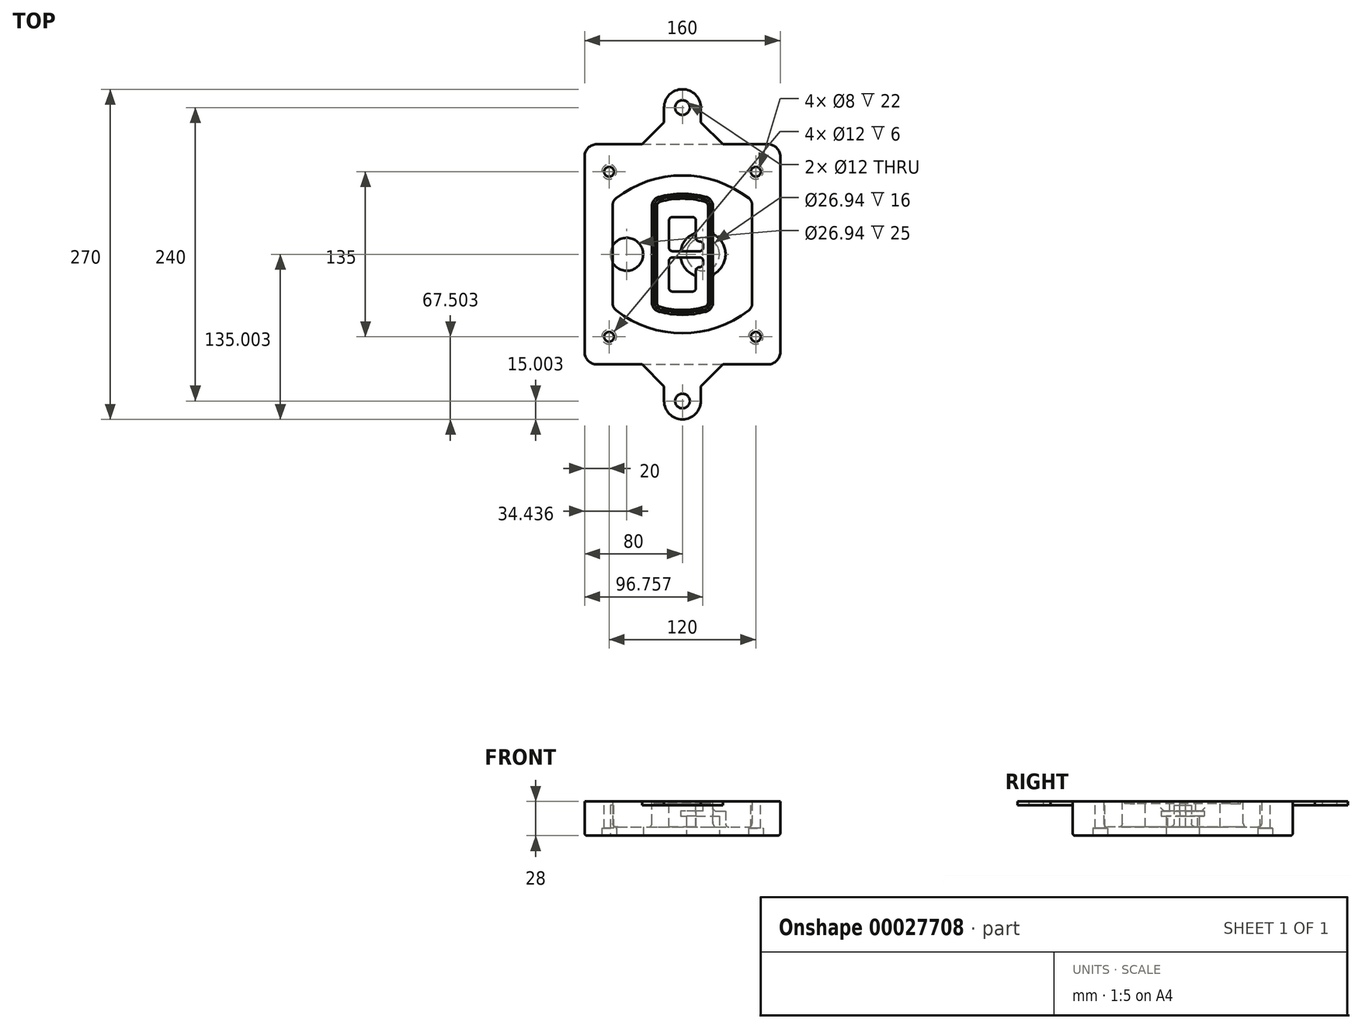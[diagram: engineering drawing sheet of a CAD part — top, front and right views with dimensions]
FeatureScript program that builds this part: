
annotation { "Feature Type Name" : "Feature", "Feature Type Description" : "" }
export const myFeature = defineFeature(function(context is Context, id is Id, definition is map)
    precondition{}
    {
        {
            var Q0;
            Q0=qCreatedBy(makeId("Top.planeOp"),FACE);
            var sketch = newSketch(context, id + "F0", { "sketchPlane" : qUnion([Q0])});
            skPoint(sketch, "E0.rect.middle", {"position": v(0, 0) * mm});
            skLineSegment(sketch, "E1.bottom", {"start": v(24.05, 28.38) * mm, "end": v(164.05, 28.38) * mm});
            skLineSegment(sketch, "E1.top", {"start": v(24.05, 208.38) * mm, "end": v(164.05, 208.38) * mm});
            skLineSegment(sketch, "E1.left", {"start": v(14.05, 38.38) * mm, "end": v(14.05, 198.38) * mm});
            skLineSegment(sketch, "E1.right", {"start": v(174.05, 38.38) * mm, "end": v(174.05, 198.38) * mm});
            skLineSegment(sketch, "E2", {"start": v(14.05, 208.38) * mm, "end": v(174.05, 28.38) * mm, "construction": true});
            skLineSegment(sketch, "E3", {"start": v(174.05, 208.38) * mm, "end": v(14.05, 28.38) * mm, "construction": true});
            skCircle(sketch, "E4", {"center": v(34.05, 185.88) * mm, "radius": 4 * mm});
            skCircle(sketch, "E5", {"center": v(154.05, 185.88) * mm, "radius": 4 * mm});
            skCircle(sketch, "E6", {"center": v(154.05, 50.88) * mm, "radius": 4 * mm});
            skCircle(sketch, "E7", {"center": v(34.05, 50.88) * mm, "radius": 4 * mm});
            skLineSegment(sketch, "E8", {"start": v(34.05, 185.88) * mm, "end": v(154.05, 185.88) * mm, "construction": true});
            skLineSegment(sketch, "E9", {"start": v(154.05, 185.88) * mm, "end": v(154.05, 50.88) * mm, "construction": true});
            skLineSegment(sketch, "E10", {"start": v(154.05, 50.88) * mm, "end": v(34.05, 50.88) * mm, "construction": true});
            skLineSegment(sketch, "E11", {"start": v(34.05, 50.88) * mm, "end": v(34.05, 185.88) * mm, "construction": true});
            skLineSegment(sketch, "E12", {"start": v(34.05, 158.68) * mm, "end": v(34.05, 78.09) * mm});
            skLineSegment(sketch, "E13", {"start": v(154.05, 158.68) * mm, "end": v(154.05, 78.09) * mm});
            skArc(sketch, "E14", {"start": v(150.2, 166.56) * mm, "mid": v(94.05, 185.88) * mm, "end": v(37.9, 166.56) * mm});
            skArc(sketch, "E15", {"start": v(37.9, 70.2) * mm, "mid": v(94.05, 50.88) * mm, "end": v(150.2, 70.2) * mm});
            skLineSegment(sketch, "E16", {"start": v(34.05, 118.38) * mm, "end": v(154.05, 118.38) * mm, "construction": true});
            skPoint(sketch, "E17.visualSharp", {"position": v(34.05, 73.38) * mm});
            skArc(sketch, "E17.filletArc", {"start": v(34.05, 78.09) * mm, "mid": v(35.06, 73.7) * mm, "end": v(37.9, 70.2) * mm});
            skPoint(sketch, "E18.visualSharp", {"position": v(34.05, 163.38) * mm});
            skArc(sketch, "E18.filletArc", {"start": v(37.9, 166.56) * mm, "mid": v(35.06, 163.06) * mm, "end": v(34.05, 158.68) * mm});
            skPoint(sketch, "E19.visualSharp", {"position": v(154.05, 163.38) * mm});
            skArc(sketch, "E19.filletArc", {"start": v(154.05, 158.68) * mm, "mid": v(153.04, 163.06) * mm, "end": v(150.2, 166.56) * mm});
            skPoint(sketch, "E20.visualSharp", {"position": v(154.05, 73.38) * mm});
            skArc(sketch, "E20.filletArc", {"start": v(150.2, 70.2) * mm, "mid": v(153.04, 73.7) * mm, "end": v(154.05, 78.09) * mm});
            skPoint(sketch, "E21.visualSharp", {"position": v(14.05, 208.38) * mm});
            skArc(sketch, "E21.filletArc", {"start": v(24.05, 208.38) * mm, "mid": v(16.98, 205.45) * mm, "end": v(14.05, 198.38) * mm});
            skPoint(sketch, "E22.visualSharp", {"position": v(174.05, 208.38) * mm});
            skArc(sketch, "E22.filletArc", {"start": v(174.05, 198.38) * mm, "mid": v(171.12, 205.45) * mm, "end": v(164.05, 208.38) * mm});
            skPoint(sketch, "E23.visualSharp", {"position": v(174.05, 28.38) * mm});
            skArc(sketch, "E23.filletArc", {"start": v(164.05, 28.38) * mm, "mid": v(171.12, 31.31) * mm, "end": v(174.05, 38.38) * mm});
            skPoint(sketch, "E24.visualSharp", {"position": v(14.05, 28.38) * mm});
            skArc(sketch, "E24.filletArc", {"start": v(14.05, 38.38) * mm, "mid": v(16.98, 31.31) * mm, "end": v(24.05, 28.38) * mm});
            skArc(sketch, "E25.0", {"start": v(151.05, 158.68) * mm, "mid": v(150.34, 161.75) * mm, "end": v(148.36, 164.2) * mm});
            skLineSegment(sketch, "E25.1", {"start": v(151.05, 158.68) * mm, "end": v(151.05, 78.09) * mm});
            skArc(sketch, "E25.2", {"start": v(148.36, 72.57) * mm, "mid": v(150.34, 75.02) * mm, "end": v(151.05, 78.09) * mm});
            skArc(sketch, "E25.3", {"start": v(39.74, 72.57) * mm, "mid": v(94.05, 53.88) * mm, "end": v(148.36, 72.57) * mm});
            skArc(sketch, "E25.4", {"start": v(37.05, 78.09) * mm, "mid": v(37.76, 75.02) * mm, "end": v(39.74, 72.57) * mm});
            skArc(sketch, "E25.5", {"start": v(148.36, 164.2) * mm, "mid": v(94.05, 182.88) * mm, "end": v(39.74, 164.2) * mm});
            skLineSegment(sketch, "E25.6", {"start": v(37.05, 158.68) * mm, "end": v(37.05, 78.09) * mm});
            skArc(sketch, "E25.7", {"start": v(39.74, 164.2) * mm, "mid": v(37.76, 161.75) * mm, "end": v(37.05, 158.68) * mm});
            skArc(sketch, "E26.0", {"start": v(35.43, 169.71) * mm, "mid": v(31.47, 164.82) * mm, "end": v(30.05, 158.68) * mm});
            skArc(sketch, "E26.1", {"start": v(152.67, 169.71) * mm, "mid": v(94.05, 189.88) * mm, "end": v(35.43, 169.71) * mm});
            skArc(sketch, "E26.2", {"start": v(158.05, 158.68) * mm, "mid": v(156.63, 164.82) * mm, "end": v(152.67, 169.71) * mm});
            skLineSegment(sketch, "E26.3", {"start": v(158.05, 158.68) * mm, "end": v(158.05, 78.09) * mm});
            skArc(sketch, "E26.4", {"start": v(152.67, 67.05) * mm, "mid": v(156.63, 71.95) * mm, "end": v(158.05, 78.09) * mm});
            skLineSegment(sketch, "E26.5", {"start": v(30.05, 158.68) * mm, "end": v(30.05, 78.09) * mm});
            skArc(sketch, "E26.6", {"start": v(35.43, 67.05) * mm, "mid": v(94.05, 46.88) * mm, "end": v(152.67, 67.05) * mm});
            skArc(sketch, "E26.7", {"start": v(30.05, 78.09) * mm, "mid": v(31.47, 71.95) * mm, "end": v(35.43, 67.05) * mm});
            skSolve(sketch);
        }
        {
            var Q0;
            Q0=makeQuery(id+"F0.imprint","IMPRINT",FACE,{"disambiguationData":[TD([[makeQuery(id+"F0.imprint","IMPRINT",EDGE,{"derivedFrom":sQuery(id+"F0.wireOp",EDGE,"E1.bottom")}),1.0]])]});
            var Q1;
            Q1=makeQuery(id+"F0.imprint","IMPRINT",FACE,{"disambiguationData":[TD([[makeQuery(id+"F0.imprint","IMPRINT",EDGE,{"derivedFrom":sQuery(id+"F0.wireOp",EDGE,"E12")}),1.0]])]});
            var Q2;
            Q2=makeQuery(id+"F0.imprint","IMPRINT",FACE,{"disambiguationData":[TD([[makeQuery(id+"F0.imprint","IMPRINT",EDGE,{"derivedFrom":sQuery(id+"F0.wireOp",EDGE,"E25.0")}),1.0]])]});
            var Q3;
            Q3=makeQuery(id+"F0.imprint","IMPRINT",FACE,{"disambiguationData":[TD([[makeQuery(id+"F0.imprint","IMPRINT",EDGE,{"derivedFrom":sQuery(id+"F0.wireOp",EDGE,"E12")}),-1.0]])]});
            extrude(context, id + "F1", {"entities" : qUnion([Q0, Q1, Q2, Q3]), "oppositeDirection" : true, "depth" : 25 * mm});
        }
        {
            var Q0;
            Q0=makeQuery(id+"F0.imprint","IMPRINT",FACE,{"disambiguationData":[TD([[makeQuery(id+"F0.imprint","IMPRINT",EDGE,{"derivedFrom":sQuery(id+"F0.wireOp",EDGE,"E12")}),1.0]])]});
            extrude(context, id + "F2", {"entities" : qUnion([Q0]), "operationType" : NewBodyOperationType.ADD, "depth" : 3 * mm});
        }
        {
            var Q0;
            Q0=makeQuery(id+"F0.imprint","IMPRINT",FACE,{"disambiguationData":[TD([[makeQuery(id+"F0.imprint","IMPRINT",EDGE,{"derivedFrom":sQuery(id+"F0.wireOp",EDGE,"E25.0")}),1.0]])]});
            extrude(context, id + "F3", {"entities" : qUnion([Q0]), "operationType" : NewBodyOperationType.REMOVE, "oppositeDirection" : true, "depth" : 18 * mm});
        }
        {
            var Q0;
            Q0=makeQuery(id+"F2.opExtrude","CAP_FACE",FACE,{"disambiguationData":[OSD([sQuery(id+"F0.wireOp",EDGE,"E12"),sQuery(id+"F0.wireOp",EDGE,"E13"),sQuery(id+"F0.wireOp",EDGE,"E14"),sQuery(id+"F0.wireOp",EDGE,"E15"),sQuery(id+"F0.wireOp",EDGE,"E17.filletArc"),sQuery(id+"F0.wireOp",EDGE,"E18.filletArc"),sQuery(id+"F0.wireOp",EDGE,"E19.filletArc"),sQuery(id+"F0.wireOp",EDGE,"E20.filletArc"),sQuery(id+"F0.wireOp",EDGE,"E25.0"),sQuery(id+"F0.wireOp",EDGE,"E25.1"),sQuery(id+"F0.wireOp",EDGE,"E25.2"),sQuery(id+"F0.wireOp",EDGE,"E25.3"),sQuery(id+"F0.wireOp",EDGE,"E25.4"),sQuery(id+"F0.wireOp",EDGE,"E25.5"),sQuery(id+"F0.wireOp",EDGE,"E25.6"),sQuery(id+"F0.wireOp",EDGE,"E25.7")])],"isStart":false});
            var sketch = newSketch(context, id + "F4", { "sketchPlane" : qUnion([Q0])});
            skArc(sketch, "E27.0", {"start": v(74.97, 71.41) * mm, "mid": v(94.05, 68.88) * mm, "end": v(113.13, 71.41) * mm});
            skArc(sketch, "E28.0", {"start": v(113.13, 165.35) * mm, "mid": v(94.05, 167.88) * mm, "end": v(74.97, 165.35) * mm});
            skLineSegment(sketch, "E29", {"start": v(69.05, 157.63) * mm, "end": v(69.05, 79.14) * mm});
            skLineSegment(sketch, "E30", {"start": v(119.05, 157.63) * mm, "end": v(119.05, 79.14) * mm});
            skLineSegment(sketch, "E31", {"start": v(69.05, 163.48) * mm, "end": v(119.05, 163.48) * mm, "construction": true});
            skLineSegment(sketch, "E32", {"start": v(69.05, 73.28) * mm, "end": v(119.05, 73.28) * mm, "construction": true});
            skPoint(sketch, "E33.visualSharp", {"position": v(69.05, 163.48) * mm});
            skArc(sketch, "E33.filletArc", {"start": v(74.97, 165.35) * mm, "mid": v(70.7, 162.5) * mm, "end": v(69.05, 157.63) * mm});
            skPoint(sketch, "E34.visualSharp", {"position": v(119.05, 163.48) * mm});
            skArc(sketch, "E34.filletArc", {"start": v(119.05, 157.63) * mm, "mid": v(117.4, 162.5) * mm, "end": v(113.13, 165.35) * mm});
            skPoint(sketch, "E35.visualSharp", {"position": v(119.05, 73.28) * mm});
            skArc(sketch, "E35.filletArc", {"start": v(113.13, 71.41) * mm, "mid": v(117.4, 74.27) * mm, "end": v(119.05, 79.14) * mm});
            skPoint(sketch, "E36.visualSharp", {"position": v(69.05, 73.28) * mm});
            skArc(sketch, "E36.filletArc", {"start": v(69.05, 79.14) * mm, "mid": v(70.7, 74.27) * mm, "end": v(74.97, 71.41) * mm});
            skArc(sketch, "E37.0", {"start": v(148.36, 164.2) * mm, "mid": v(94.05, 182.88) * mm, "end": v(39.74, 164.2) * mm});
            skArc(sketch, "E37.1", {"start": v(39.74, 164.2) * mm, "mid": v(37.76, 161.75) * mm, "end": v(37.05, 158.68) * mm});
            skLineSegment(sketch, "E37.2", {"start": v(37.05, 158.68) * mm, "end": v(37.05, 78.09) * mm});
            skArc(sketch, "E37.3", {"start": v(37.05, 78.09) * mm, "mid": v(37.76, 75.02) * mm, "end": v(39.74, 72.57) * mm});
            skArc(sketch, "E37.4", {"start": v(39.74, 72.57) * mm, "mid": v(94.05, 53.88) * mm, "end": v(148.36, 72.57) * mm});
            skArc(sketch, "E37.5", {"start": v(148.36, 72.57) * mm, "mid": v(150.34, 75.02) * mm, "end": v(151.05, 78.09) * mm});
            skLineSegment(sketch, "E37.6", {"start": v(151.05, 158.68) * mm, "end": v(151.05, 78.09) * mm});
            skArc(sketch, "E37.7", {"start": v(151.05, 158.68) * mm, "mid": v(150.34, 161.75) * mm, "end": v(148.36, 164.2) * mm});
            skLineSegment(sketch, "E38.0", {"start": v(117.05, 157.63) * mm, "end": v(117.05, 79.14) * mm});
            skArc(sketch, "E38.1", {"start": v(112.61, 73.34) * mm, "mid": v(115.81, 75.49) * mm, "end": v(117.05, 79.14) * mm});
            skArc(sketch, "E38.2", {"start": v(75.49, 73.34) * mm, "mid": v(94.05, 70.88) * mm, "end": v(112.61, 73.34) * mm});
            skArc(sketch, "E38.3", {"start": v(71.05, 79.14) * mm, "mid": v(72.29, 75.49) * mm, "end": v(75.49, 73.34) * mm});
            skLineSegment(sketch, "E38.4", {"start": v(71.05, 157.63) * mm, "end": v(71.05, 79.14) * mm});
            skArc(sketch, "E38.5", {"start": v(117.05, 157.63) * mm, "mid": v(115.81, 161.28) * mm, "end": v(112.61, 163.42) * mm});
            skArc(sketch, "E38.6", {"start": v(75.49, 163.42) * mm, "mid": v(72.29, 161.28) * mm, "end": v(71.05, 157.63) * mm});
            skArc(sketch, "E38.7", {"start": v(112.61, 163.42) * mm, "mid": v(94.05, 165.88) * mm, "end": v(75.49, 163.42) * mm});
            skArc(sketch, "E39.0", {"start": v(115.05, 157.63) * mm, "mid": v(114.23, 160.06) * mm, "end": v(112.1, 161.5) * mm});
            skLineSegment(sketch, "E39.1", {"start": v(115.05, 157.63) * mm, "end": v(115.05, 79.14) * mm});
            skArc(sketch, "E39.2", {"start": v(112.1, 75.27) * mm, "mid": v(114.23, 76.7) * mm, "end": v(115.05, 79.14) * mm});
            skArc(sketch, "E39.3", {"start": v(76, 75.27) * mm, "mid": v(94.05, 72.88) * mm, "end": v(112.1, 75.27) * mm});
            skArc(sketch, "E39.4", {"start": v(73.05, 79.14) * mm, "mid": v(73.87, 76.7) * mm, "end": v(76, 75.27) * mm});
            skArc(sketch, "E39.5", {"start": v(112.1, 161.5) * mm, "mid": v(94.05, 163.88) * mm, "end": v(76, 161.5) * mm});
            skLineSegment(sketch, "E39.6", {"start": v(73.05, 157.63) * mm, "end": v(73.05, 79.14) * mm});
            skArc(sketch, "E39.7", {"start": v(76, 161.5) * mm, "mid": v(73.87, 160.06) * mm, "end": v(73.05, 157.63) * mm});
            skLineSegment(sketch, "E40", {"start": v(69.05, 118.38) * mm, "end": v(119.05, 118.38) * mm, "construction": true});
            skLineSegment(sketch, "E41", {"start": v(83.05, 123.88) * mm, "end": v(83.05, 145.88) * mm});
            skLineSegment(sketch, "E42", {"start": v(86.05, 148.88) * mm, "end": v(102.05, 148.88) * mm});
            skLineSegment(sketch, "E43", {"start": v(105.05, 145.88) * mm, "end": v(105.05, 131.88) * mm});
            skLineSegment(sketch, "E44", {"start": v(108.05, 128.88) * mm, "end": v(108.05, 128.88) * mm});
            skLineSegment(sketch, "E45", {"start": v(111.05, 125.88) * mm, "end": v(111.05, 123.88) * mm});
            skLineSegment(sketch, "E46", {"start": v(108.05, 120.88) * mm, "end": v(86.05, 120.88) * mm});
            skPoint(sketch, "E47.visualSharp", {"position": v(83.05, 148.88) * mm});
            skArc(sketch, "E47.filletArc", {"start": v(86.05, 148.88) * mm, "mid": v(83.93, 148) * mm, "end": v(83.05, 145.88) * mm});
            skPoint(sketch, "E48.visualSharp", {"position": v(105.05, 148.88) * mm});
            skArc(sketch, "E48.filletArc", {"start": v(105.05, 145.88) * mm, "mid": v(104.17, 148) * mm, "end": v(102.05, 148.88) * mm});
            skPoint(sketch, "E49.visualSharp", {"position": v(105.05, 128.88) * mm});
            skArc(sketch, "E49.filletArc", {"start": v(105.05, 131.88) * mm, "mid": v(105.93, 129.76) * mm, "end": v(108.05, 128.88) * mm});
            skPoint(sketch, "E50.visualSharp", {"position": v(111.05, 128.88) * mm});
            skArc(sketch, "E50.filletArc", {"start": v(111.05, 125.88) * mm, "mid": v(110.17, 128) * mm, "end": v(108.05, 128.88) * mm});
            skPoint(sketch, "E51.visualSharp", {"position": v(111.05, 120.88) * mm});
            skArc(sketch, "E51.filletArc", {"start": v(108.05, 120.88) * mm, "mid": v(110.17, 121.76) * mm, "end": v(111.05, 123.88) * mm});
            skPoint(sketch, "E52.visualSharp", {"position": v(83.05, 120.88) * mm});
            skArc(sketch, "E52.filletArc", {"start": v(83.05, 123.88) * mm, "mid": v(83.93, 121.76) * mm, "end": v(86.05, 120.88) * mm});
            skLineSegment(sketch, "E53.0.MirrorCS", {"start": v(108.05, 115.88) * mm, "end": v(86.05, 115.88) * mm});
            skArc(sketch, "E54.0.MirrorCS", {"start": v(83.05, 112.88) * mm, "mid": v(83.93, 115) * mm, "end": v(86.05, 115.88) * mm});
            skLineSegment(sketch, "E55.0.MirrorCS", {"start": v(83.05, 112.88) * mm, "end": v(83.05, 90.88) * mm});
            skArc(sketch, "E56.0.MirrorCS", {"start": v(86.05, 87.88) * mm, "mid": v(83.93, 88.76) * mm, "end": v(83.05, 90.88) * mm});
            skLineSegment(sketch, "E57.0.MirrorCS", {"start": v(86.05, 87.88) * mm, "end": v(102.05, 87.88) * mm});
            skArc(sketch, "E58.0.MirrorCS", {"start": v(105.05, 90.88) * mm, "mid": v(104.17, 88.76) * mm, "end": v(102.05, 87.88) * mm});
            skLineSegment(sketch, "E59.0.MirrorCS", {"start": v(105.05, 90.88) * mm, "end": v(105.05, 104.88) * mm});
            skArc(sketch, "E60.0.MirrorCS", {"start": v(105.05, 104.88) * mm, "mid": v(105.93, 107) * mm, "end": v(108.05, 107.88) * mm});
            skArc(sketch, "E61.0.MirrorCS", {"start": v(111.05, 110.88) * mm, "mid": v(110.17, 108.76) * mm, "end": v(108.05, 107.88) * mm});
            skLineSegment(sketch, "E62.0.MirrorCS", {"start": v(111.05, 110.88) * mm, "end": v(111.05, 112.88) * mm});
            skArc(sketch, "E63.0.MirrorCS", {"start": v(108.05, 115.88) * mm, "mid": v(110.17, 115) * mm, "end": v(111.05, 112.88) * mm});
            skSolve(sketch);
        }
        {
            var Q0;
            Q0=makeQuery(id+"F4.imprint","IMPRINT",FACE,{"disambiguationData":[TD([[makeQuery(id+"F4.imprint","IMPRINT",EDGE,{"derivedFrom":sQuery(id+"F4.wireOp",EDGE,"E27.0")}),1.0]])]});
            var Q1;
            Q1=makeQuery(id+"F4.imprint","IMPRINT",FACE,{"disambiguationData":[TD([[makeQuery(id+"F4.imprint","IMPRINT",EDGE,{"derivedFrom":sQuery(id+"F4.wireOp",EDGE,"E38.0")}),-1.0]])]});
            var Q2;
            Q2=makeQuery(id+"F4.imprint","IMPRINT",FACE,{"disambiguationData":[TD([[makeQuery(id+"F4.imprint","IMPRINT",EDGE,{"derivedFrom":sQuery(id+"F4.wireOp",EDGE,"E39.0")}),1.0]])]});
            extrude(context, id + "F5", {"entities" : qUnion([Q0, Q1, Q2]), "operationType" : NewBodyOperationType.ADD, "endBound" : BoundingType.UP_TO_NEXT, "oppositeDirection" : true, "depth" : 25 * mm});
        }
        {
            var Q0;
            Q0=makeQuery(id+"F4.imprint","IMPRINT",FACE,{"disambiguationData":[TD([[makeQuery(id+"F4.imprint","IMPRINT",EDGE,{"derivedFrom":sQuery(id+"F4.wireOp",EDGE,"E38.0")}),-1.0]])]});
            extrude(context, id + "F6", {"entities" : qUnion([Q0]), "operationType" : NewBodyOperationType.REMOVE, "oppositeDirection" : true, "depth" : 2 * mm});
        }
        {
            var Q0;
            Q0=makeQuery(id+"F1.opExtrude","CAP_FACE",FACE,{"disambiguationData":[OSD([sQuery(id+"F0.wireOp",EDGE,"E1.bottom"),sQuery(id+"F0.wireOp",EDGE,"E1.top"),sQuery(id+"F0.wireOp",EDGE,"E1.left"),sQuery(id+"F0.wireOp",EDGE,"E1.right"),sQuery(id+"F0.wireOp",EDGE,"E4"),sQuery(id+"F0.wireOp",EDGE,"E5"),sQuery(id+"F0.wireOp",EDGE,"E6"),sQuery(id+"F0.wireOp",EDGE,"E7"),sQuery(id+"F0.wireOp",EDGE,"E21.filletArc"),sQuery(id+"F0.wireOp",EDGE,"E22.filletArc"),sQuery(id+"F0.wireOp",EDGE,"E23.filletArc"),sQuery(id+"F0.wireOp",EDGE,"E24.filletArc")])],"isStart":false});
            var sketch = newSketch(context, id + "F7", { "sketchPlane" : qUnion([Q0])});
            skCircle(sketch, "E64", {"center": v(110.8, -118.38) * mm, "radius": 13.47 * mm});
            skCircle(sketch, "E65", {"center": v(48.49, -118.38) * mm, "radius": 13.47 * mm});
            skLineSegment(sketch, "E66", {"start": v(174.05, -118.38) * mm, "end": v(14.05, -118.38) * mm});
            skCircle(sketch, "E67", {"center": v(110.8, -118.38) * mm, "radius": 18.47 * mm});
            skCircle(sketch, "E68", {"center": v(154.05, -185.88) * mm, "radius": 6 * mm});
            skCircle(sketch, "E69", {"center": v(34.05, -185.88) * mm, "radius": 6 * mm});
            skCircle(sketch, "E70", {"center": v(34.05, -50.88) * mm, "radius": 6 * mm});
            skCircle(sketch, "E71", {"center": v(154.05, -50.88) * mm, "radius": 6 * mm});
            skSolve(sketch);
        }
        {
            var Q0;
            {var subQ1=sQuery(id+"F7.wireOp",EDGE,"E66");var subQ4=sQuery(id+"F7.wireOp",EDGE,"E64");var subQ6=makeQuery(id+"F7.imprint","INTERSECT",VERTEX,{"disambiguationData":[OD(0.0)],"derivedFrom":[subQ4,subQ1]});Q0=makeQuery(id+"F7.imprint","IMPRINT",FACE,{"disambiguationData":[TD([[makeQuery(id+"F7.imprint","IMPRINT",EDGE,{"disambiguationData":[TD([[subQ6,-1.0]])],"derivedFrom":subQ4}),-1.0]])]});}
            var Q1;
            {var subQ0=sQuery(id+"F7.wireOp",EDGE,"E66");var subQ1=sQuery(id+"F7.wireOp",EDGE,"E64");var subQ3=makeQuery(id+"F7.imprint","INTERSECT",VERTEX,{"disambiguationData":[OD(0.0)],"derivedFrom":[subQ1,subQ0]});Q1=makeQuery(id+"F7.imprint","IMPRINT",FACE,{"disambiguationData":[TD([[makeQuery(id+"F7.imprint","IMPRINT",EDGE,{"disambiguationData":[TD([[subQ3,-1.0]])],"derivedFrom":subQ1}),1.0]])]});}
            var Q2;
            {var subQ0=sQuery(id+"F7.wireOp",EDGE,"E66");var subQ1=sQuery(id+"F7.wireOp",EDGE,"E64");var subQ3=makeQuery(id+"F7.imprint","INTERSECT",VERTEX,{"disambiguationData":[OD(0.0)],"derivedFrom":[subQ1,subQ0]});Q2=makeQuery(id+"F7.imprint","IMPRINT",FACE,{"disambiguationData":[TD([[makeQuery(id+"F7.imprint","IMPRINT",EDGE,{"disambiguationData":[TD([[subQ3,1.0]])],"derivedFrom":subQ1}),1.0]])]});}
            var Q3;
            {var subQ1=sQuery(id+"F7.wireOp",EDGE,"E66");var subQ4=sQuery(id+"F7.wireOp",EDGE,"E64");var subQ6=makeQuery(id+"F7.imprint","INTERSECT",VERTEX,{"disambiguationData":[OD(0.0)],"derivedFrom":[subQ4,subQ1]});Q3=makeQuery(id+"F7.imprint","IMPRINT",FACE,{"disambiguationData":[TD([[makeQuery(id+"F7.imprint","IMPRINT",EDGE,{"disambiguationData":[TD([[subQ6,1.0]])],"derivedFrom":subQ4}),-1.0]])]});}
            extrude(context, id + "F8", {"entities" : qUnion([Q0, Q1, Q2, Q3]), "operationType" : NewBodyOperationType.ADD, "oppositeDirection" : true, "depth" : 20 * mm});
        }
        {
            var Q0;
            {var subQ0=sQuery(id+"F7.wireOp",EDGE,"E66");var subQ1=sQuery(id+"F7.wireOp",EDGE,"E64");var subQ3=makeQuery(id+"F7.imprint","INTERSECT",VERTEX,{"disambiguationData":[OD(0.0)],"derivedFrom":[subQ1,subQ0]});Q0=makeQuery(id+"F7.imprint","IMPRINT",FACE,{"disambiguationData":[TD([[makeQuery(id+"F7.imprint","IMPRINT",EDGE,{"disambiguationData":[TD([[subQ3,-1.0]])],"derivedFrom":subQ1}),1.0]])]});}
            var Q1;
            {var subQ0=sQuery(id+"F7.wireOp",EDGE,"E66");var subQ1=sQuery(id+"F7.wireOp",EDGE,"E64");var subQ3=makeQuery(id+"F7.imprint","INTERSECT",VERTEX,{"disambiguationData":[OD(0.0)],"derivedFrom":[subQ1,subQ0]});Q1=makeQuery(id+"F7.imprint","IMPRINT",FACE,{"disambiguationData":[TD([[makeQuery(id+"F7.imprint","IMPRINT",EDGE,{"disambiguationData":[TD([[subQ3,1.0]])],"derivedFrom":subQ1}),1.0]])]});}
            extrude(context, id + "F9", {"entities" : qUnion([Q0, Q1]), "operationType" : NewBodyOperationType.REMOVE, "oppositeDirection" : true, "depth" : 16 * mm});
        }
        {
            var Q0;
            {var subQ0=sQuery(id+"F7.wireOp",EDGE,"E66");var subQ1=sQuery(id+"F7.wireOp",EDGE,"E65");var subQ3=makeQuery(id+"F7.imprint","INTERSECT",VERTEX,{"disambiguationData":[OD(0.0)],"derivedFrom":[subQ1,subQ0]});Q0=makeQuery(id+"F7.imprint","IMPRINT",FACE,{"disambiguationData":[TD([[makeQuery(id+"F7.imprint","IMPRINT",EDGE,{"disambiguationData":[TD([[subQ3,-1.0]])],"derivedFrom":subQ1}),1.0]])]});}
            var Q1;
            {var subQ0=sQuery(id+"F7.wireOp",EDGE,"E66");var subQ1=sQuery(id+"F7.wireOp",EDGE,"E65");var subQ3=makeQuery(id+"F7.imprint","INTERSECT",VERTEX,{"disambiguationData":[OD(0.0)],"derivedFrom":[subQ1,subQ0]});Q1=makeQuery(id+"F7.imprint","IMPRINT",FACE,{"disambiguationData":[TD([[makeQuery(id+"F7.imprint","IMPRINT",EDGE,{"disambiguationData":[TD([[subQ3,1.0]])],"derivedFrom":subQ1}),1.0]])]});}
            extrude(context, id + "F10", {"entities" : qUnion([Q0, Q1]), "operationType" : NewBodyOperationType.REMOVE, "oppositeDirection" : true, "depth" : 25 * mm});
        }
        {
            var Q0;
            Q0=makeQuery(id+"F7.imprint","IMPRINT",FACE,{"disambiguationData":[TD([[makeQuery(id+"F7.imprint","IMPRINT",EDGE,{"derivedFrom":sQuery(id+"F7.wireOp",EDGE,"E68")}),1.0]])]});
            var Q1;
            Q1=makeQuery(id+"F7.imprint","IMPRINT",FACE,{"disambiguationData":[TD([[makeQuery(id+"F7.imprint","IMPRINT",EDGE,{"derivedFrom":makeQuery(id+"F1.opExtrude","CAP_EDGE",EDGE,{"disambiguationData":[OSD([sQuery(id+"F0.wireOp",EDGE,"E5")])],"isStart":false})}),-1.0]])]});
            var Q2;
            Q2=makeQuery(id+"F7.imprint","IMPRINT",FACE,{"disambiguationData":[TD([[makeQuery(id+"F7.imprint","IMPRINT",EDGE,{"derivedFrom":sQuery(id+"F7.wireOp",EDGE,"E69")}),1.0]])]});
            var Q3;
            Q3=makeQuery(id+"F7.imprint","IMPRINT",FACE,{"disambiguationData":[TD([[makeQuery(id+"F7.imprint","IMPRINT",EDGE,{"derivedFrom":makeQuery(id+"F1.opExtrude","CAP_EDGE",EDGE,{"disambiguationData":[OSD([sQuery(id+"F0.wireOp",EDGE,"E4")])],"isStart":false})}),-1.0]])]});
            var Q4;
            Q4=makeQuery(id+"F7.imprint","IMPRINT",FACE,{"disambiguationData":[TD([[makeQuery(id+"F7.imprint","IMPRINT",EDGE,{"derivedFrom":sQuery(id+"F7.wireOp",EDGE,"E70")}),1.0]])]});
            var Q5;
            Q5=makeQuery(id+"F7.imprint","IMPRINT",FACE,{"disambiguationData":[TD([[makeQuery(id+"F7.imprint","IMPRINT",EDGE,{"derivedFrom":makeQuery(id+"F1.opExtrude","CAP_EDGE",EDGE,{"disambiguationData":[OSD([sQuery(id+"F0.wireOp",EDGE,"E7")])],"isStart":false})}),-1.0]])]});
            var Q6;
            Q6=makeQuery(id+"F7.imprint","IMPRINT",FACE,{"disambiguationData":[TD([[makeQuery(id+"F7.imprint","IMPRINT",EDGE,{"derivedFrom":sQuery(id+"F7.wireOp",EDGE,"E71")}),1.0]])]});
            var Q7;
            Q7=makeQuery(id+"F7.imprint","IMPRINT",FACE,{"disambiguationData":[TD([[makeQuery(id+"F7.imprint","IMPRINT",EDGE,{"derivedFrom":makeQuery(id+"F1.opExtrude","CAP_EDGE",EDGE,{"disambiguationData":[OSD([sQuery(id+"F0.wireOp",EDGE,"E6")])],"isStart":false})}),-1.0]])]});
            extrude(context, id + "F11", {"entities" : qUnion([Q0, Q1, Q2, Q3, Q4, Q5, Q6, Q7]), "operationType" : NewBodyOperationType.REMOVE, "oppositeDirection" : true, "depth" : 6 * mm});
        }
        {
            var Q0;
            Q0=makeQuery(id+"F9.boolean.opBoolean","COPY",FACE,{"derivedFrom":makeQuery(id+"F9.opExtrude","CAP_FACE",FACE,{"disambiguationData":[OSD([sQuery(id+"F7.wireOp",EDGE,"E64")])],"isStart":false})});
            var sketch = newSketch(context, id + "F12", { "sketchPlane" : qUnion([Q0])});
            skArc(sketch, "E72.0", {"start": v(105.05, -100.83) * mm, "mid": v(96.62, -106.56) * mm, "end": v(92.5, -115.88) * mm});
            skArc(sketch, "E72.1", {"start": v(92.5, -120.88) * mm, "mid": v(96.62, -130.2) * mm, "end": v(105.05, -135.93) * mm});
            skLineSegment(sketch, "E73", {"start": v(92.5, -120.88) * mm, "end": v(108.05, -120.88) * mm});
            skLineSegment(sketch, "E74.0", {"start": v(108.05, -115.88) * mm, "end": v(92.5, -115.88) * mm});
            skArc(sketch, "E74.1", {"start": v(108.05, -115.88) * mm, "mid": v(110.17, -115) * mm, "end": v(111.05, -112.88) * mm});
            skLineSegment(sketch, "E74.2", {"start": v(111.05, -110.88) * mm, "end": v(111.05, -112.88) * mm});
            skArc(sketch, "E74.3", {"start": v(111.05, -110.88) * mm, "mid": v(110.17, -108.76) * mm, "end": v(108.05, -107.88) * mm});
            skArc(sketch, "E74.4", {"start": v(105.05, -104.88) * mm, "mid": v(105.93, -107) * mm, "end": v(108.05, -107.88) * mm});
            skLineSegment(sketch, "E74.5", {"start": v(105.05, -100.83) * mm, "end": v(105.05, -104.88) * mm});
            skLineSegment(sketch, "E74.7", {"start": v(108.05, -120.88) * mm, "end": v(92.5, -120.88) * mm});
            skArc(sketch, "E74.8", {"start": v(108.05, -120.88) * mm, "mid": v(110.17, -121.76) * mm, "end": v(111.05, -123.88) * mm});
            skLineSegment(sketch, "E74.9", {"start": v(111.05, -125.88) * mm, "end": v(111.05, -123.88) * mm});
            skArc(sketch, "E74.10", {"start": v(111.05, -125.88) * mm, "mid": v(110.17, -128) * mm, "end": v(108.05, -128.88) * mm});
            skArc(sketch, "E74.11", {"start": v(105.05, -131.88) * mm, "mid": v(105.93, -129.76) * mm, "end": v(108.05, -128.88) * mm});
            skLineSegment(sketch, "E74.12", {"start": v(105.05, -135.93) * mm, "end": v(105.05, -131.88) * mm});
            skPoint(sketch, "E75.orphan", {"position": v(105.05, -145.88) * mm});
            skPoint(sketch, "E76.orphan", {"position": v(86.05, -120.88) * mm});
            skPoint(sketch, "E77.orphan", {"position": v(86.05, -115.88) * mm});
            skPoint(sketch, "E78.orphan", {"position": v(105.05, -90.88) * mm});
            skSolve(sketch);
        }
        {
            var Q0;
            {var subQ7=sQuery(id+"F12.wireOp",EDGE,"E72.0");var subQ14=sQuery(id+"F12.wireOp",EDGE,"E72.1");var subQ16=sQuery(id+"F12.wireOp",EDGE,"E74.1");var subQ18=sQuery(id+"F12.wireOp",EDGE,"E74.8");Q0=qUnion([makeQuery(id+"F12.imprint","IMPRINT",FACE,{"disambiguationData":[TD([[makeQuery(id+"F12.imprint","IMPRINT",EDGE,{"derivedFrom":subQ7}),1.0]])]}),makeQuery(id+"F12.imprint","IMPRINT",FACE,{"disambiguationData":[TD([[makeQuery(id+"F12.imprint","IMPRINT",EDGE,{"derivedFrom":subQ14}),1.0]])]}),makeQuery(id+"F12.imprint","IMPRINT",FACE,{"disambiguationData":[TD([[makeQuery(id+"F12.imprint","IMPRINT",EDGE,{"derivedFrom":subQ16}),1.0]])]}),makeQuery(id+"F12.imprint","IMPRINT",FACE,{"disambiguationData":[TD([[makeQuery(id+"F12.imprint","IMPRINT",EDGE,{"derivedFrom":subQ18}),-1.0]])]})]);}
            var Q1;
            Q1=makeQuery(id+"F5.boolean.opBoolean","SPLIT",FACE,{"disambiguationData":[TD([makeQuery(id+"F5.opExtrude","SWEPT_FACE",FACE,{"disambiguationData":[OSD([sQuery(id+"F4.wireOp",EDGE,"E41")])]})])],"derivedFrom":makeQuery(id+"F3.boolean.opBoolean","COPY",FACE,{"derivedFrom":makeQuery(id+"F3.opExtrude","CAP_FACE",FACE,{"disambiguationData":[OSD([sQuery(id+"F0.wireOp",EDGE,"E25.0"),sQuery(id+"F0.wireOp",EDGE,"E25.1"),sQuery(id+"F0.wireOp",EDGE,"E25.2"),sQuery(id+"F0.wireOp",EDGE,"E25.3"),sQuery(id+"F0.wireOp",EDGE,"E25.4"),sQuery(id+"F0.wireOp",EDGE,"E25.5"),sQuery(id+"F0.wireOp",EDGE,"E25.6"),sQuery(id+"F0.wireOp",EDGE,"E25.7")])],"isStart":false})})});
            extrude(context, id + "F13", {"entities" : qUnion([Q0]), "operationType" : NewBodyOperationType.REMOVE, "endBound" : BoundingType.UP_TO_SURFACE, "endBoundEntityFace" : qUnion([Q1]), "depth" : 25 * mm});
        }
        {
            var Q0;
            Q0=makeQuery(id+"F3.boolean.opBoolean","COPY",EDGE,{"derivedFrom":makeQuery(id+"F3.opExtrude","CAP_EDGE",EDGE,{"disambiguationData":[OSD([sQuery(id+"F0.wireOp",EDGE,"E25.6")])],"isStart":false})});
            var Q1;
            Q1=makeQuery(id+"F8.boolean.opBoolean","INTERSECT",EDGE,{"derivedFrom":[makeQuery(id+"F5.opExtrude","SWEPT_FACE",FACE,{"disambiguationData":[OSD([sQuery(id+"F4.wireOp",EDGE,"E30")])]}),makeQuery(id+"F8.opExtrude","CAP_FACE",FACE,{"disambiguationData":[OSD([sQuery(id+"F7.wireOp",EDGE,"E67")])],"isStart":false})]});
            var Q2;
            Q2=makeQuery(id+"F8.boolean.opBoolean","INTERSECT",EDGE,{"disambiguationData":[OD(1.0)],"derivedFrom":[makeQuery(id+"F5.opExtrude","SWEPT_FACE",FACE,{"disambiguationData":[OSD([sQuery(id+"F4.wireOp",EDGE,"E30")])]}),makeQuery(id+"F8.opExtrude","SWEPT_FACE",FACE,{"disambiguationData":[OSD([sQuery(id+"F7.wireOp",EDGE,"E67")])]})]});
            var Q3;
            {var subQ0=sQuery(id+"F4.wireOp",EDGE,"E30");Q3=makeQuery(id+"F8.boolean.opBoolean","SPLIT",EDGE,{"disambiguationData":[TD([makeQuery(id+"F5.opExtrude","SWEPT_FACE",FACE,{"disambiguationData":[OSD([sQuery(id+"F4.wireOp",EDGE,"E35.filletArc")])]})])],"derivedFrom":makeQuery(id+"F5.opExtrude","CAP_EDGE",EDGE,{"disambiguationData":[OSD([subQ0])],"isStart":false})});}
            var Q4;
            {var subQ0=sQuery(id+"F0.wireOp",EDGE,"E25.7");var subQ1=sQuery(id+"F0.wireOp",EDGE,"E25.1");var subQ2=sQuery(id+"F0.wireOp",EDGE,"E25.6");var subQ3=sQuery(id+"F0.wireOp",EDGE,"E25.5");var subQ4=sQuery(id+"F0.wireOp",EDGE,"E25.4");var subQ5=sQuery(id+"F0.wireOp",EDGE,"E25.0");var subQ6=sQuery(id+"F0.wireOp",EDGE,"E25.2");var subQ7=sQuery(id+"F0.wireOp",EDGE,"E25.3");Q4=makeQuery(id+"F8.boolean.opBoolean","INTERSECT",EDGE,{"derivedFrom":[makeQuery(id+"F5.boolean.opBoolean","SPLIT",FACE,{"disambiguationData":[TD([makeQuery(id+"F2.opExtrude","SWEPT_FACE",FACE,{"disambiguationData":[OSD([subQ5])]})])],"derivedFrom":makeQuery(id+"F3.boolean.opBoolean","COPY",FACE,{"derivedFrom":makeQuery(id+"F3.opExtrude","CAP_FACE",FACE,{"disambiguationData":[OSD([subQ5,subQ1,subQ6,subQ7,subQ4,subQ3,subQ2,subQ0])],"isStart":false})})}),makeQuery(id+"F8.opExtrude","SWEPT_FACE",FACE,{"disambiguationData":[OSD([sQuery(id+"F7.wireOp",EDGE,"E67")])]})]});}
            var Q5;
            Q5=makeQuery(id+"F8.boolean.opBoolean","INTERSECT",EDGE,{"disambiguationData":[OD(0.0)],"derivedFrom":[makeQuery(id+"F5.opExtrude","SWEPT_FACE",FACE,{"disambiguationData":[OSD([sQuery(id+"F4.wireOp",EDGE,"E30")])]}),makeQuery(id+"F8.opExtrude","SWEPT_FACE",FACE,{"disambiguationData":[OSD([sQuery(id+"F7.wireOp",EDGE,"E67")])]})]});
            fillet(context, id + "F14", {"entities" : qUnion([Q0, Q1, Q2, Q3, Q4, Q5]), "radius" : 3 * mm, "tangentPropagation" : true, "allowEdgeOverflow" : false});
        }
        {
            var Q0;
            Q0=makeQuery(id+"F1.opExtrude","CAP_EDGE",EDGE,{"disambiguationData":[OSD([sQuery(id+"F0.wireOp",EDGE,"E1.bottom")])],"isStart":false});
            fillet(context, id + "F15", {"entities" : qUnion([Q0]), "radius" : 2 * mm, "tangentPropagation" : true, "allowEdgeOverflow" : false});
        }
        {
            var Q0;
            {var subQ0=sQuery(id+"F0.wireOp",EDGE,"E1.bottom");var subQ1=sQuery(id+"F0.wireOp",EDGE,"E1.top");var subQ2=sQuery(id+"F0.wireOp",EDGE,"E1.left");var subQ3=sQuery(id+"F0.wireOp",EDGE,"E1.right");var subQ4=sQuery(id+"F0.wireOp",EDGE,"E4");var subQ5=sQuery(id+"F0.wireOp",EDGE,"E5");var subQ6=sQuery(id+"F0.wireOp",EDGE,"E6");var subQ7=sQuery(id+"F0.wireOp",EDGE,"E7");var subQ8=sQuery(id+"F0.wireOp",EDGE,"E21.filletArc");var subQ9=sQuery(id+"F0.wireOp",EDGE,"E22.filletArc");var subQ10=sQuery(id+"F0.wireOp",EDGE,"E23.filletArc");var subQ11=sQuery(id+"F0.wireOp",EDGE,"E24.filletArc");Q0=makeQuery(id+"F2.boolean.opBoolean","SPLIT",FACE,{"disambiguationData":[TD([makeQuery(id+"F1.opExtrude","SWEPT_FACE",FACE,{"disambiguationData":[OSD([subQ0])]})])],"derivedFrom":makeQuery(id+"F1.opExtrude","CAP_FACE",FACE,{"disambiguationData":[OSD([subQ0,subQ1,subQ2,subQ3,subQ4,subQ5,subQ6,subQ7,subQ8,subQ9,subQ10,subQ11])],"isStart":true})});}
            var sketch = newSketch(context, id + "F16", { "sketchPlane" : qUnion([Q0])});
            skLineSegment(sketch, "E79", {"start": v(94.05, 208.38) * mm, "end": v(94.05, 238.38) * mm, "construction": true});
            skCircle(sketch, "E80", {"center": v(94.05, 238.38) * mm, "radius": 6 * mm});
            skArc(sketch, "E81", {"start": v(109.05, 238.38) * mm, "mid": v(94.05, 253.38) * mm, "end": v(79.05, 238.38) * mm});
            skLineSegment(sketch, "E82", {"start": v(79.05, 238.38) * mm, "end": v(79.05, 226.38) * mm});
            skLineSegment(sketch, "E83", {"start": v(109.05, 238.38) * mm, "end": v(109.05, 226.38) * mm});
            skLineSegment(sketch, "E84", {"start": v(109.05, 226.38) * mm, "end": v(127.05, 208.38) * mm});
            skLineSegment(sketch, "E85", {"start": v(79.05, 226.38) * mm, "end": v(61.05, 208.38) * mm});
            skLineSegment(sketch, "E86", {"start": v(14.05, 118.38) * mm, "end": v(174.05, 118.38) * mm, "construction": true});
            skLineSegment(sketch, "E87.MirrorCS", {"start": v(79.05, 10.38) * mm, "end": v(61.05, 28.38) * mm});
            skLineSegment(sketch, "E88.MirrorCS", {"start": v(79.05, -1.62) * mm, "end": v(79.05, 10.38) * mm});
            skArc(sketch, "E89.MirrorCS", {"start": v(109.05, -1.62) * mm, "mid": v(94.05, -16.62) * mm, "end": v(79.05, -1.62) * mm});
            skLineSegment(sketch, "E90.MirrorCS", {"start": v(109.05, -1.62) * mm, "end": v(109.05, 10.38) * mm});
            skLineSegment(sketch, "E91.MirrorCS", {"start": v(109.05, 10.38) * mm, "end": v(127.05, 28.38) * mm});
            skCircle(sketch, "E92.MirrorC", {"center": v(94.05, -1.62) * mm, "radius": 6 * mm});
            skSolve(sketch);
        }
        {
            var Q0;
            Q0=makeQuery(id+"F16.imprint","IMPRINT",FACE,{"disambiguationData":[TD([[makeQuery(id+"F16.imprint","IMPRINT",EDGE,{"derivedFrom":sQuery(id+"F16.wireOp",EDGE,"E80")}),-1.0]])]});
            var Q1;
            Q1=makeQuery(id+"F16.imprint","IMPRINT",FACE,{"disambiguationData":[TD([[makeQuery(id+"F16.imprint","IMPRINT",EDGE,{"derivedFrom":makeQuery(id+"F1.opExtrude","CAP_EDGE",EDGE,{"disambiguationData":[OSD([sQuery(id+"F0.wireOp",EDGE,"E1.left")])],"isStart":true})}),-1.0]])]});
            var Q2;
            {var subQ2=sQuery(id+"F16.wireOp",EDGE,"E87.MirrorCS");Q2=makeQuery(id+"F16.imprint","IMPRINT",FACE,{"disambiguationData":[TD([[makeQuery(id+"F16.imprint","IMPRINT",EDGE,{"derivedFrom":subQ2}),-1.0]])]});}
            var Q3;
            Q3=makeQuery(id+"F2.opExtrude","CAP_FACE",FACE,{"disambiguationData":[OSD([sQuery(id+"F0.wireOp",EDGE,"E12"),sQuery(id+"F0.wireOp",EDGE,"E13"),sQuery(id+"F0.wireOp",EDGE,"E14"),sQuery(id+"F0.wireOp",EDGE,"E15"),sQuery(id+"F0.wireOp",EDGE,"E17.filletArc"),sQuery(id+"F0.wireOp",EDGE,"E18.filletArc"),sQuery(id+"F0.wireOp",EDGE,"E19.filletArc"),sQuery(id+"F0.wireOp",EDGE,"E20.filletArc"),sQuery(id+"F0.wireOp",EDGE,"E25.0"),sQuery(id+"F0.wireOp",EDGE,"E25.1"),sQuery(id+"F0.wireOp",EDGE,"E25.2"),sQuery(id+"F0.wireOp",EDGE,"E25.3"),sQuery(id+"F0.wireOp",EDGE,"E25.4"),sQuery(id+"F0.wireOp",EDGE,"E25.5"),sQuery(id+"F0.wireOp",EDGE,"E25.6"),sQuery(id+"F0.wireOp",EDGE,"E25.7")])],"isStart":false});
            extrude(context, id + "F17", {"entities" : qUnion([Q0, Q1, Q2]), "operationType" : NewBodyOperationType.ADD, "endBound" : BoundingType.UP_TO_SURFACE, "endBoundEntityFace" : qUnion([Q3]), "depth" : 25 * mm});
        }
    });
